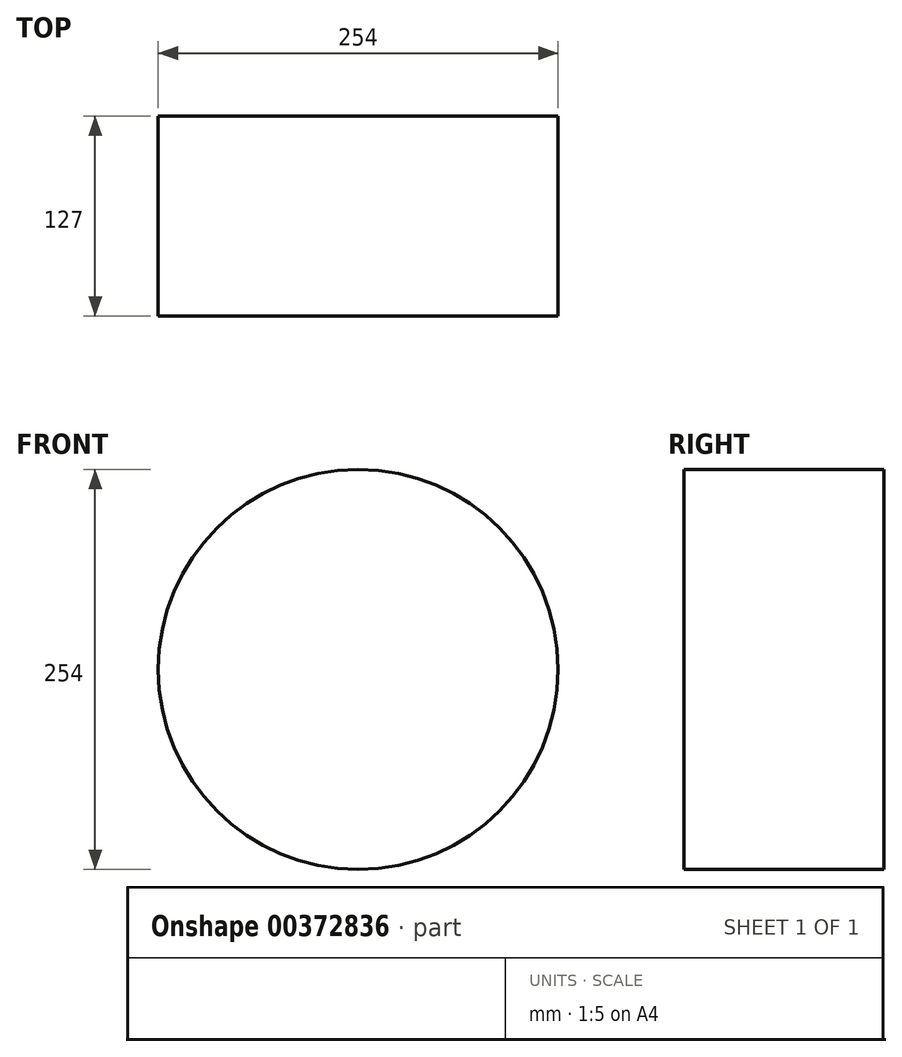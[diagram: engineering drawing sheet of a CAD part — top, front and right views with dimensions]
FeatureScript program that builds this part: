
annotation { "Feature Type Name" : "Feature", "Feature Type Description" : "" }
export const myFeature = defineFeature(function(context is Context, id is Id, definition is map)
    precondition{}
    {
        {
            var Q0;
            Q0=qCreatedBy(makeId("Front.planeOp"),FACE);
            var sketch = newSketch(context, id + "F0", { "sketchPlane" : qUnion([Q0])});
            skCircle(sketch, "E0", {"center": v(0, 0) * mm, "radius": 127 * mm});
            skSolve(sketch);
        }
        {
            var Q0;
            Q0 = qSketchRegion(id + "F0", true);
            extrude(context, id + "F1", {"entities" : qUnion([Q0]), "depth" : 127 * mm});
        }
    });
